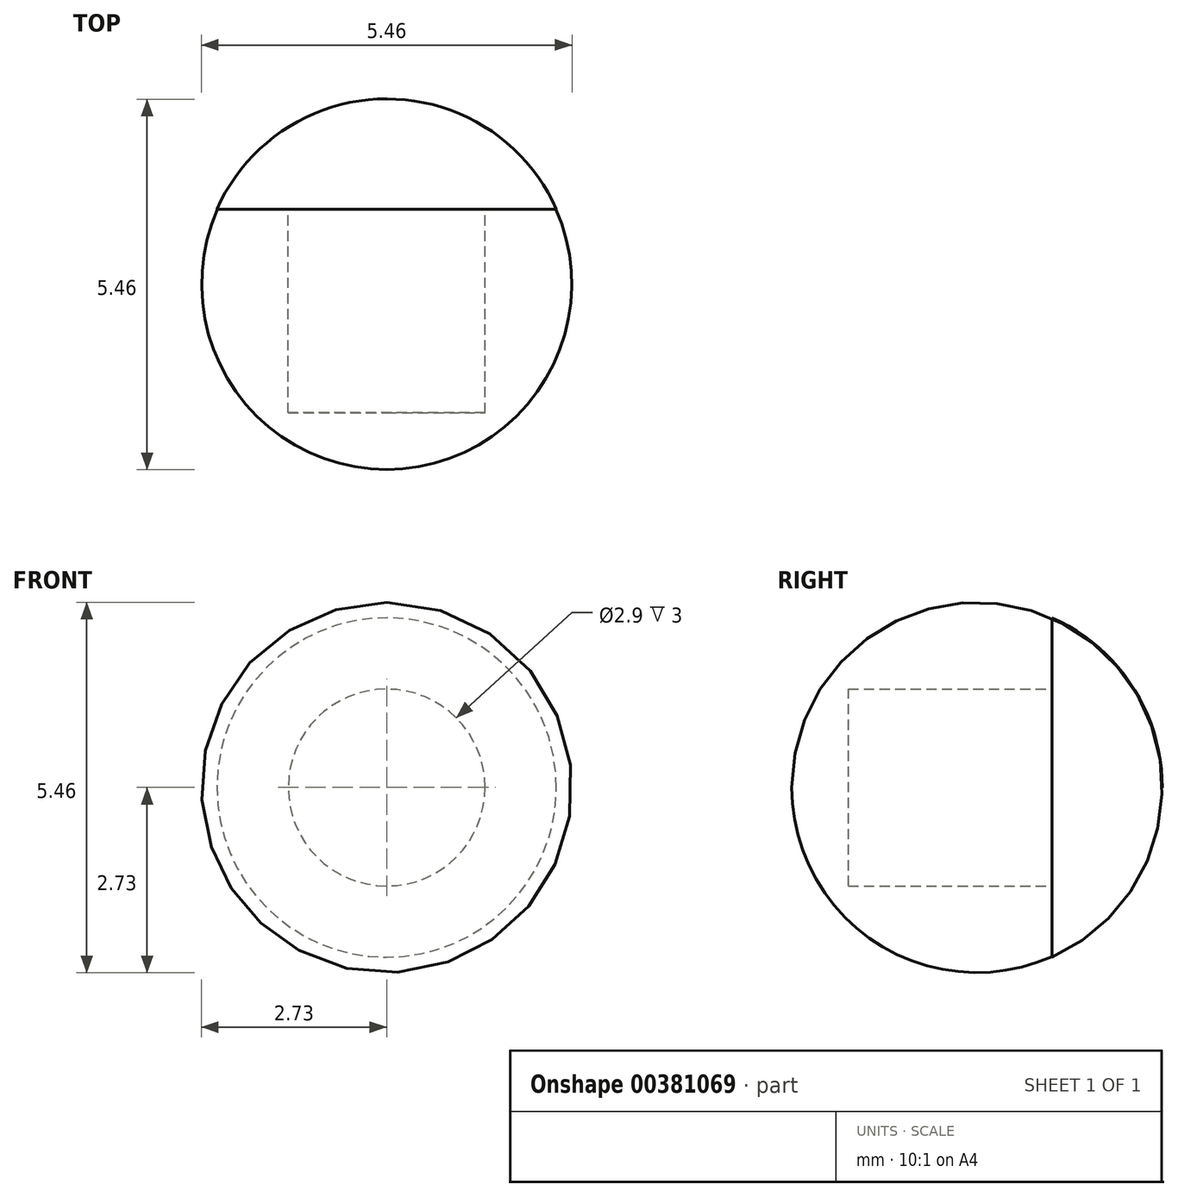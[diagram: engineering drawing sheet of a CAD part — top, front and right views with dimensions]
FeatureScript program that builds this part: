
annotation { "Feature Type Name" : "Feature", "Feature Type Description" : "" }
export const myFeature = defineFeature(function(context is Context, id is Id, definition is map)
    precondition{}
    {
        {
            var Q0;
            Q0=qCreatedBy(makeId("Top.planeOp"),FACE);
            var sketch = newSketch(context, id + "F0", { "sketchPlane" : qUnion([Q0])});
            skLineSegment(sketch, "E0", {"start": v(0, 0) * mm, "end": v(-2.5, 0) * mm});
            skLineSegment(sketch, "E1", {"start": v(0, 0) * mm, "end": v(0, 1.62) * mm});
            skArc(sketch, "E2", {"start": v(0, 1.62) * mm, "mid": v(-1.5, 1.18) * mm, "end": v(-2.5, 0) * mm});
            skSolve(sketch);
        }
        {
            var Q0;
            {var subQ0=sQuery(id+"F0.wireOp",EDGE,"E0");Q0=makeQuery(id+"F0.imprint","IMPRINT",FACE,{"disambiguationData":[TD([[makeQuery(id+"F0.imprint","IMPRINT",EDGE,{"derivedFrom":subQ0}),-1.0]])]});}
            var Q1;
            {var subQ0=sQuery(id+"F0.wireOp",EDGE,"8CnxaPGg-786o-oRZ0-JlNl-uUl5FRue14oA");Q1=makeQuery(id+"F0.imprint","IMPRINT",FACE,{"disambiguationData":[TD([[makeQuery(id+"F0.imprint","IMPRINT",EDGE,{"derivedFrom":subQ0}),1.0]])]});}
            var Q2;
            Q2=sQuery(id+"F0.wireOp",EDGE,"E1");
            revolve(context, id + "F1", {"entities" : qUnion([Q0, Q1]), "axis" : qUnion([Q2]), "revolveType" : RevolveType.FULL});
        }
        {
            var Q0;
            Q0=makeQuery(id+"F1.opRevolve","SWEPT_FACE",FACE,{"disambiguationData":[OSD([sQuery(id+"F0.wireOp",EDGE,"E0")])]});
            var sketch = newSketch(context, id + "F2", { "sketchPlane" : qUnion([Q0])});
            skCircle(sketch, "E3", {"center": v(0, 0) * mm, "radius": 1.45 * mm});
            skSolve(sketch);
        }
        {
            var Q0;
            Q0 = qSketchRegion(id + "F2", true);
            extrude(context, id + "F3", {"entities" : qUnion([Q0]), "operationType" : NewBodyOperationType.ADD, "depth" : 3 * mm});
        }
    });
